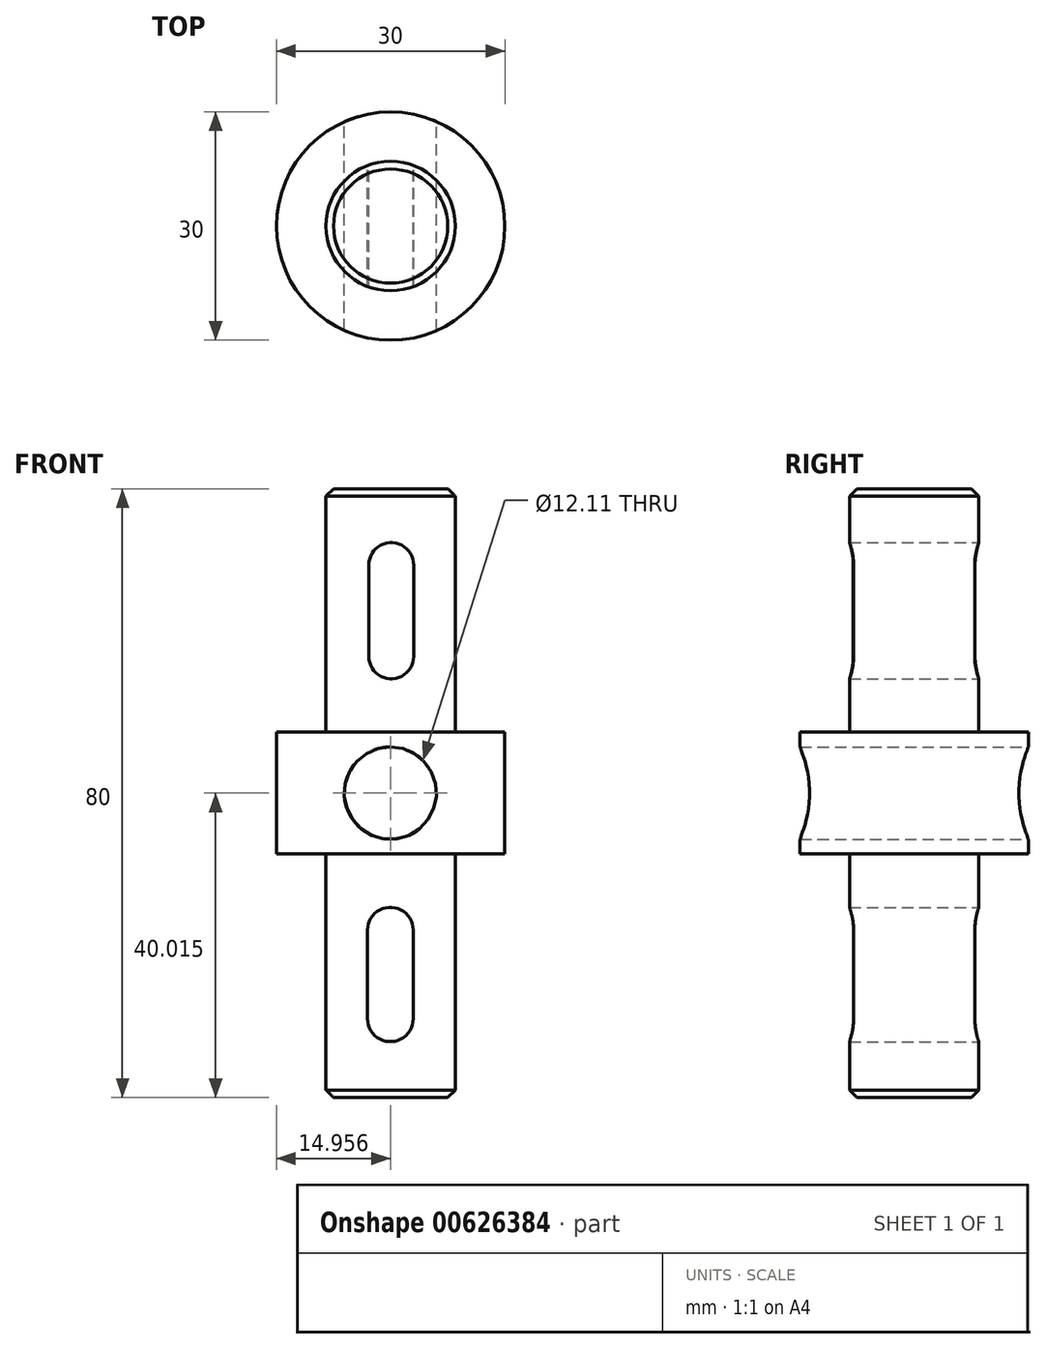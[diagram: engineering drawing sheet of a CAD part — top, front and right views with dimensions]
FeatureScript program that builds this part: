
annotation { "Feature Type Name" : "Feature", "Feature Type Description" : "" }
export const myFeature = defineFeature(function(context is Context, id is Id, definition is map)
    precondition{}
    {
        {
            var Q0;
            Q0=qCreatedBy(makeId("Top.planeOp"),FACE);
            var sketch = newSketch(context, id + "F0", { "sketchPlane" : qUnion([Q0])});
            skCircle(sketch, "E0", {"center": v(-31.74, 24.02) * mm, "radius": 8.5 * mm});
            skSolve(sketch);
        }
        {
            var Q0;
            Q0 = qSketchRegion(id + "F0", true);
            extrude(context, id + "F1", {"entities" : qUnion([Q0]), "depth" : 32 * mm, "offsetDistance" : 25 * mm});
        }
        {
            var Q0;
            Q0=qCreatedBy(makeId("Front.planeOp"),FACE);
            cPlane(context, id + "F2", {"entities" : qUnion([Q0]), "cplaneType" : CPlaneType.OFFSET, "offset" : 33 * mm, "oppositeDirection" : true, "width" : 150 * mm, "height" : 150 * mm});
        }
        {
            var Q0;
            Q0=qCreatedBy(id+"F2.planeOp",FACE);
            var sketch = newSketch(context, id + "F3", { "sketchPlane" : qUnion([Q0])});
            skPoint(sketch, "E1.orphan", {"position": v(-23.2, 0) * mm});
            skPoint(sketch, "E2.end.orphan", {"position": v(-40.13, 31.87) * mm});
            skPoint(sketch, "E3.end.orphan", {"position": v(-40.13, 0) * mm});
            skLineSegment(sketch, "E4", {"start": v(-34.63, 21.96) * mm, "end": v(-34.63, 9.96) * mm});
            skArc(sketch, "E5", {"start": v(-34.63, 9.96) * mm, "mid": v(-31.68, 7.02) * mm, "end": v(-28.74, 9.96) * mm});
            skArc(sketch, "E6", {"start": v(-28.74, 21.96) * mm, "mid": v(-31.68, 24.91) * mm, "end": v(-34.63, 21.96) * mm});
            skPoint(sketch, "E7.orphan", {"position": v(-34.63, 0) * mm});
            skPoint(sketch, "E8.orphan", {"position": v(-28.63, 0) * mm});
            skPoint(sketch, "E9.end.orphan", {"position": v(-28.63, 37.26) * mm});
            skPoint(sketch, "E10.end.orphan", {"position": v(-40.13, 37.26) * mm});
            skLineSegment(sketch, "E11", {"start": v(-28.74, 9.96) * mm, "end": v(-28.74, 21.96) * mm});
            skSolve(sketch);
        }
        {
            var Q0;
            Q0 = qSketchRegion(id + "F3", true);
            extrude(context, id + "F4", {"entities" : qUnion([Q0]), "operationType" : NewBodyOperationType.REMOVE, "depth" : 32.4 * mm, "offsetDistance" : 25 * mm});
        }
        {
            var Q0;
            Q0=makeQuery(id+"F1.opExtrude","CAP_EDGE",EDGE,{"disambiguationData":[OSD([sQuery(id+"F0.wireOp",EDGE,"E0")])],"isStart":false});
            chamfer(context, id + "F5", {"entities" : qUnion([Q0]), "width" : 1 * mm, "tangentPropagation" : true});
        }
        {
            var Q0;
            Q0=makeQuery(id+"F1.opExtrude","CAP_FACE",FACE,{"disambiguationData":[OSD([sQuery(id+"F0.wireOp",EDGE,"E0")])],"isStart":true});
            var sketch = newSketch(context, id + "F6", { "sketchPlane" : qUnion([Q0])});
            skCircle(sketch, "E12", {"center": v(-31.74, -24.02) * mm, "radius": 15 * mm});
            skSolve(sketch);
        }
        {
            var Q0;
            Q0 = qSketchRegion(id + "F6", true);
            extrude(context, id + "F7", {"entities" : qUnion([Q0]), "operationType" : NewBodyOperationType.ADD, "depth" : 16 * mm, "offsetDistance" : 25 * mm});
        }
        {
            var Q0;
            Q0=makeQuery(id+"F7.opExtrude","CAP_FACE",FACE,{"disambiguationData":[OSD([sQuery(id+"F6.wireOp",EDGE,"E12")])],"isStart":false});
            var sketch = newSketch(context, id + "F8", { "sketchPlane" : qUnion([Q0])});
            skCircle(sketch, "E13", {"center": v(-31.74, -24.02) * mm, "radius": 8.5 * mm});
            skSolve(sketch);
        }
        {
            var Q0;
            Q0 = qSketchRegion(id + "F8", true);
            extrude(context, id + "F9", {"entities" : qUnion([Q0]), "operationType" : NewBodyOperationType.ADD, "depth" : 32 * mm, "offsetDistance" : 25 * mm});
        }
        {
            var Q0;
            Q0=makeQuery(id+"F9.opExtrude","CAP_EDGE",EDGE,{"disambiguationData":[OSD([sQuery(id+"F8.wireOp",EDGE,"E13")])],"isStart":false});
            chamfer(context, id + "F10", {"entities" : qUnion([Q0]), "width" : 1 * mm, "tangentPropagation" : true});
        }
        {
            var Q0;
            Q0=qCreatedBy(makeId("Front.planeOp"),FACE);
            cPlane(context, id + "F11", {"entities" : qUnion([Q0]), "cplaneType" : CPlaneType.OFFSET, "offset" : 35.2 * mm, "oppositeDirection" : true, "width" : 150 * mm, "height" : 150 * mm});
        }
        {
            var Q0;
            Q0=qCreatedBy(id+"F11.planeOp",FACE);
            var sketch = newSketch(context, id + "F12", { "sketchPlane" : qUnion([Q0])});
            skArc(sketch, "E14", {"start": v(-28.79, -26) * mm, "mid": v(-31.79, -23) * mm, "end": v(-34.79, -26) * mm});
            skArc(sketch, "E15", {"start": v(-34.79, -37.64) * mm, "mid": v(-31.79, -40.64) * mm, "end": v(-28.79, -37.64) * mm});
            skPoint(sketch, "E16.orphan", {"position": v(-40.07, -46.6) * mm});
            skPoint(sketch, "E17.orphan", {"position": v(-23.43, -16.9) * mm});
            skPoint(sketch, "E18.orphan", {"position": v(-40.07, -16.9) * mm});
            skLineSegment(sketch, "E19", {"start": v(-28.79, -37.64) * mm, "end": v(-28.79, -26) * mm});
            skLineSegment(sketch, "E20", {"start": v(-34.79, -37.64) * mm, "end": v(-34.79, -26) * mm});
            skSolve(sketch);
        }
        {
            var Q0;
            Q0 = qSketchRegion(id + "F12", true);
            extrude(context, id + "F13", {"entities" : qUnion([Q0]), "operationType" : NewBodyOperationType.REMOVE, "depth" : 46.1 * mm, "offsetDistance" : 25 * mm});
        }
        {
            var Q0;
            Q0=qCreatedBy(id+"F11.planeOp",FACE);
            cPlane(context, id + "F14", {"entities" : qUnion([Q0]), "cplaneType" : CPlaneType.OFFSET, "offset" : 6.2 * mm, "oppositeDirection" : true, "width" : 150 * mm, "height" : 150 * mm});
        }
        {
            var Q0;
            Q0=qCreatedBy(id+"F14.planeOp",FACE);
            var sketch = newSketch(context, id + "F15", { "sketchPlane" : qUnion([Q0])});
            skCircle(sketch, "E21", {"center": v(-31.78, -7.99) * mm, "radius": 6.06 * mm});
            skPoint(sketch, "E22.orphan", {"position": v(-16.75, 0) * mm});
            skPoint(sketch, "E23.orphan", {"position": v(-16.68, -15.99) * mm});
            skPoint(sketch, "E24.orphan", {"position": v(-46.86, 0) * mm});
            skPoint(sketch, "E25.orphan", {"position": v(-46.86, -15.99) * mm});
            skSolve(sketch);
        }
        {
            var Q0;
            Q0 = qSketchRegion(id + "F15", true);
            extrude(context, id + "F16", {"entities" : qUnion([Q0]), "operationType" : NewBodyOperationType.REMOVE, "depth" : 53.1 * mm, "offsetDistance" : 25 * mm});
        }
    });
